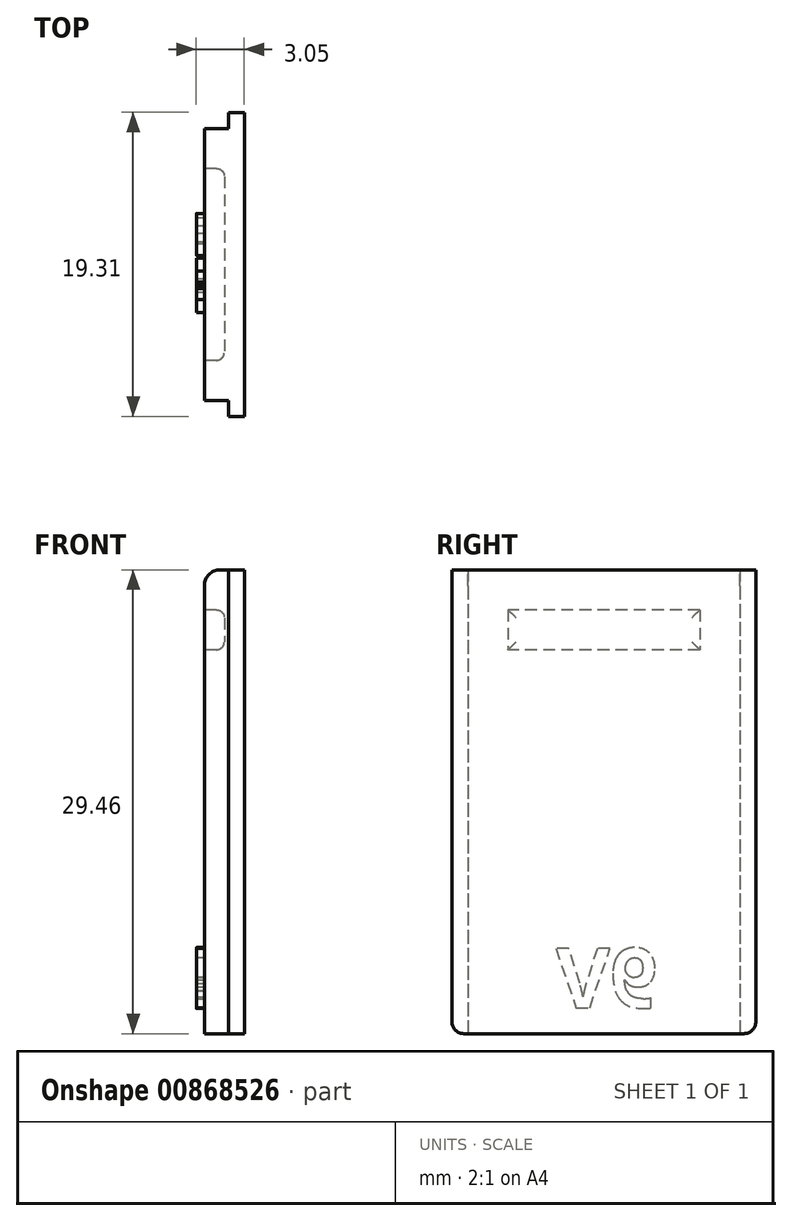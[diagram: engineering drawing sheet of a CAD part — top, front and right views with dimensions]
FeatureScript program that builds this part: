
annotation { "Feature Type Name" : "Feature", "Feature Type Description" : "" }
export const myFeature = defineFeature(function(context is Context, id is Id, definition is map)
    precondition{}
    {
        {
            var Q0;
            Q0=qCreatedBy(makeId("Top.planeOp"),FACE);
            var sketch = newSketch(context, id + "F0", { "sketchPlane" : qUnion([Q0])});
            skLineSegment(sketch, "E0.bottom", {"start": v(10.04, 3.88) * mm, "end": v(11.57, 3.88) * mm});
            skLineSegment(sketch, "E0.top", {"start": v(10.04, -13.4) * mm, "end": v(11.57, -13.4) * mm});
            skLineSegment(sketch, "E0.left", {"start": v(10.04, 3.88) * mm, "end": v(10.04, -13.4) * mm});
            skLineSegment(sketch, "E0.right", {"start": v(12.58, 3.88) * mm, "end": v(12.58, -13.4) * mm});
            skLineSegment(sketch, "E1.top", {"start": v(12.58, 4.9) * mm, "end": v(11.57, 4.9) * mm});
            skLineSegment(sketch, "E1.left", {"start": v(12.58, 3.88) * mm, "end": v(12.58, 4.9) * mm});
            skLineSegment(sketch, "E1.right", {"start": v(11.57, 3.88) * mm, "end": v(11.57, 4.9) * mm});
            skLineSegment(sketch, "E2.top", {"start": v(12.58, -14.4) * mm, "end": v(11.57, -14.4) * mm});
            skLineSegment(sketch, "E2.left", {"start": v(12.58, -13.4) * mm, "end": v(12.58, -14.4) * mm});
            skLineSegment(sketch, "E2.right", {"start": v(11.57, -13.4) * mm, "end": v(11.57, -14.4) * mm});
            skSolve(sketch);
        }
        {
            var Q0;
            Q0 = qSketchRegion(id + "F0", true);
            extrude(context, id + "F1", {"entities" : qUnion([Q0]), "depth" : 29.46 * mm, "offsetDistance" : 25.4 * mm});
        }
        {
            var Q0;
            Q0=makeQuery(id+"F1.opExtrude","SWEPT_FACE",FACE,{"disambiguationData":[OSD([sQuery(id+"F0.wireOp",EDGE,"E0.left")])]});
            var sketch = newSketch(context, id + "F2", { "sketchPlane" : qUnion([Q0])});
            skLineSegment(sketch, "E3.bottom", {"start": v(-1.34, 26.92) * mm, "end": v(10.85, 26.92) * mm});
            skLineSegment(sketch, "E3.top", {"start": v(-1.34, 24.38) * mm, "end": v(10.85, 24.38) * mm});
            skLineSegment(sketch, "E3.left", {"start": v(-1.34, 26.92) * mm, "end": v(-1.34, 24.38) * mm});
            skLineSegment(sketch, "E3.right", {"start": v(10.85, 26.92) * mm, "end": v(10.85, 24.38) * mm});
            skSolve(sketch);
        }
        {
            var Q0;
            Q0 = qSketchRegion(id + "F2", true);
            extrude(context, id + "F3", {"entities" : qUnion([Q0]), "operationType" : NewBodyOperationType.REMOVE, "oppositeDirection" : true, "depth" : 1.27 * mm, "offsetDistance" : 25.4 * mm});
        }
        {
            var Q0;
            Q0=makeQuery(id+"F3.boolean.opBoolean","COPY",FACE,{"derivedFrom":makeQuery(id+"F3.opExtrude","CAP_FACE",FACE,{"disambiguationData":[OSD([sQuery(id+"F2.wireOp",EDGE,"E3.bottom"),sQuery(id+"F2.wireOp",EDGE,"E3.top"),sQuery(id+"F2.wireOp",EDGE,"E3.left"),sQuery(id+"F2.wireOp",EDGE,"E3.right")])],"isStart":false})});
            fillet(context, id + "F4", {"entities" : qUnion([Q0]), "radius" : 0.5 * mm, "tangentPropagation" : true, "allowEdgeOverflow" : false});
        }
        {
            var Q0;
            Q0=makeQuery(id+"F1.opExtrude","CAP_EDGE",EDGE,{"disambiguationData":[OSD([sQuery(id+"F0.wireOp",EDGE,"E0.left")])],"isStart":false});
            fillet(context, id + "F5", {"entities" : qUnion([Q0]), "radius" : 1.02 * mm, "tangentPropagation" : true, "allowEdgeOverflow" : false});
        }
        {
            var Q0;
            Q0=makeQuery(id+"F1.opExtrude","SWEPT_FACE",FACE,{"disambiguationData":[OSD([sQuery(id+"F0.wireOp",EDGE,"E0.left")])]});
            var sketch = newSketch(context, id + "F6", { "sketchPlane" : qUnion([Q0])});
            skText(sketch, "E4", { "text": "9V", "fontName": "OpenSans-Bold.ttf"});
            const initialGuessF6  = {"E4": [0.00135, 0.00165, 1, 0, 0.00381]};
            skSetInitialGuess(sketch, initialGuessF6);
            skSolve(sketch);
        }
        {
            var Q0;
            Q0 = qSketchRegion(id + "F6", true);
            extrude(context, id + "F7", {"entities" : qUnion([Q0]), "operationType" : NewBodyOperationType.ADD, "depth" : 0.5 * mm, "offsetDistance" : 25.4 * mm});
        }
        {
            var Q0;
            Q0=makeQuery(id+"F1.opExtrude","CAP_EDGE",EDGE,{"disambiguationData":[OSD([sQuery(id+"F0.wireOp",EDGE,"E1.top")])],"isStart":true});
            var Q1;
            Q1=makeQuery(id+"F1.opExtrude","CAP_EDGE",EDGE,{"disambiguationData":[OSD([sQuery(id+"F0.wireOp",EDGE,"E2.top")])],"isStart":true});
            fillet(context, id + "F8", {"entities" : qUnion([Q0, Q1]), "radius" : 0.76 * mm, "tangentPropagation" : true, "allowEdgeOverflow" : false});
        }
    });
